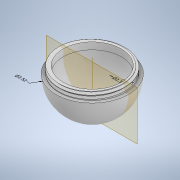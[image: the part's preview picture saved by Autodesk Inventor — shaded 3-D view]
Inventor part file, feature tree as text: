
AUTODESK INVENTOR PART (.ipt)
format: ipt  version: 2022 (Build 260153000, 153)  size: 269,312 bytes
history: native  units: in
note: dims shown in document units (in); Inventor stores cm internally (conversion verified against a paired STEP export)
features: other x4, sketch x3, revolve x1, thicken_offset x1, shell x1, extrude x1, plane x1, helix x1, projected_geometry x1
ambient origin geometry x8: Origin, YZ Plane, XZ Plane, XY Plane, X Axis, Y Axis, Z Axis, Center Point
bodies: Solid1 (feature_tree)
feature tree (14):
  other  "Annotations"
  revolve  "Revolution1"  [1 undecoded]
  thicken_offset  "Thicken1"
  shell  "Shell2"  Thickness=0.25in
  extrude  "Extrusion1"  Depth=2.3in
  plane  "Work Plane1"
  sketch  "Sketch3"  dims[d32=0.025in d35=60.0deg d36=0.1117in d39=0.125in d40=0.3in d41=0.3937in d42=0.0in d43=90.0deg d44=90.0deg d45=0.0in d46=0.0in d12=0.3434in d13=0.1773in d14=-0.1569in d15=2.3in d16=0.4123in d17=2.52in d4=0.0344in]
  other  "Work Axis1"
  helix  "Coil1"  [1 undecoded]
  sketch  "Sketch1"  dims[d3=90.0deg d5=0.26in d6=0.25in d7=0.25in]
  sketch  "Sketch2"  dims[d10=0.24in d11=0.0in d18=2.3in d23=0.0in]
  projected_geometry  "Projected Loop1"
  other  "Diameter Dimension 1"
  other  "Diameter Dimension 2"
note: 2 required parameter values undecoded (feature->parameter linkage not recoverable at this tier; creation-order binding heuristic only, values carry confidence <= 0.55)